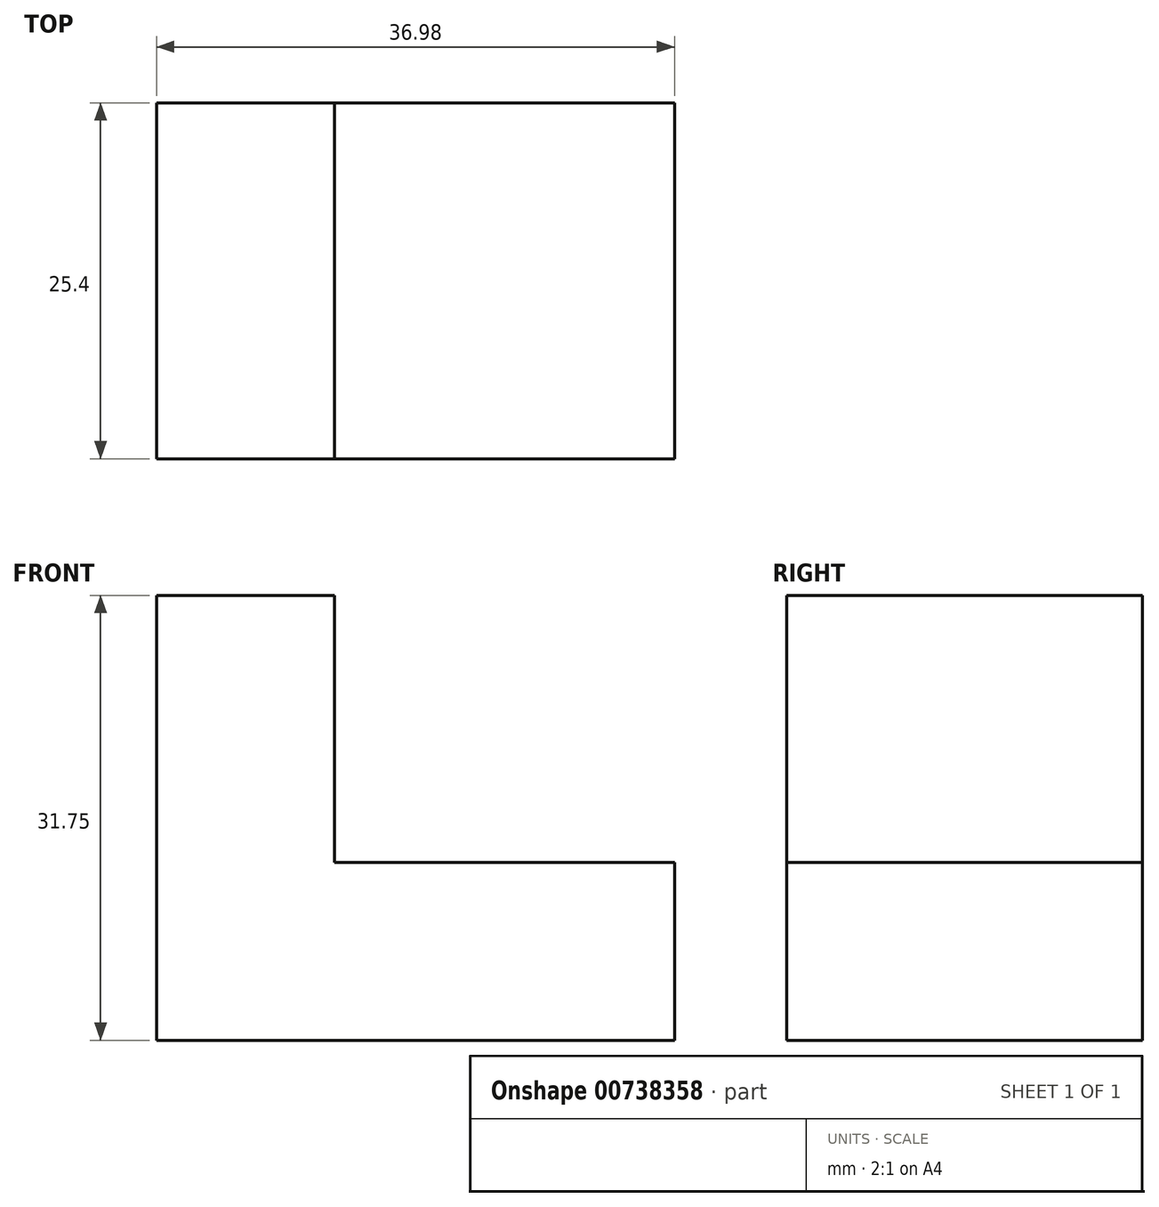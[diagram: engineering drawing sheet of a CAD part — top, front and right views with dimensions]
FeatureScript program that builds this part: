
annotation { "Feature Type Name" : "Feature", "Feature Type Description" : "" }
export const myFeature = defineFeature(function(context is Context, id is Id, definition is map)
    precondition{}
    {
        {
            var Q0;
            Q0=qCreatedBy(makeId("Front.planeOp"),FACE);
            var sketch = newSketch(context, id + "F0", { "sketchPlane" : qUnion([Q0])});
            skLineSegment(sketch, "E0", {"start": v(0, 31.75) * mm, "end": v(0, 0) * mm});
            skLineSegment(sketch, "E1", {"start": v(0, 0) * mm, "end": v(38.1, 0) * mm});
            skLineSegment(sketch, "E2", {"start": v(36.98, 0) * mm, "end": v(36.98, 12.7) * mm});
            skLineSegment(sketch, "E3", {"start": v(36.98, 12.7) * mm, "end": v(12.7, 12.7) * mm});
            skLineSegment(sketch, "E4", {"start": v(12.7, 12.7) * mm, "end": v(12.7, 31.75) * mm});
            skLineSegment(sketch, "E5", {"start": v(12.7, 31.75) * mm, "end": v(0, 31.75) * mm});
            skSolve(sketch);
        }
        {
            var Q0;
            {var subQ2=sQuery(id+"F0.wireOp",EDGE,"E0");Q0=makeQuery(id+"F0.imprint","IMPRINT",FACE,{"disambiguationData":[TD([[makeQuery(id+"F0.imprint","IMPRINT",EDGE,{"derivedFrom":subQ2}),1.0]])]});}
            extrude(context, id + "F1", {"entities" : qUnion([Q0]), "depth" : 25.4 * mm, "offsetDistance" : 25.4 * mm});
        }
    });
